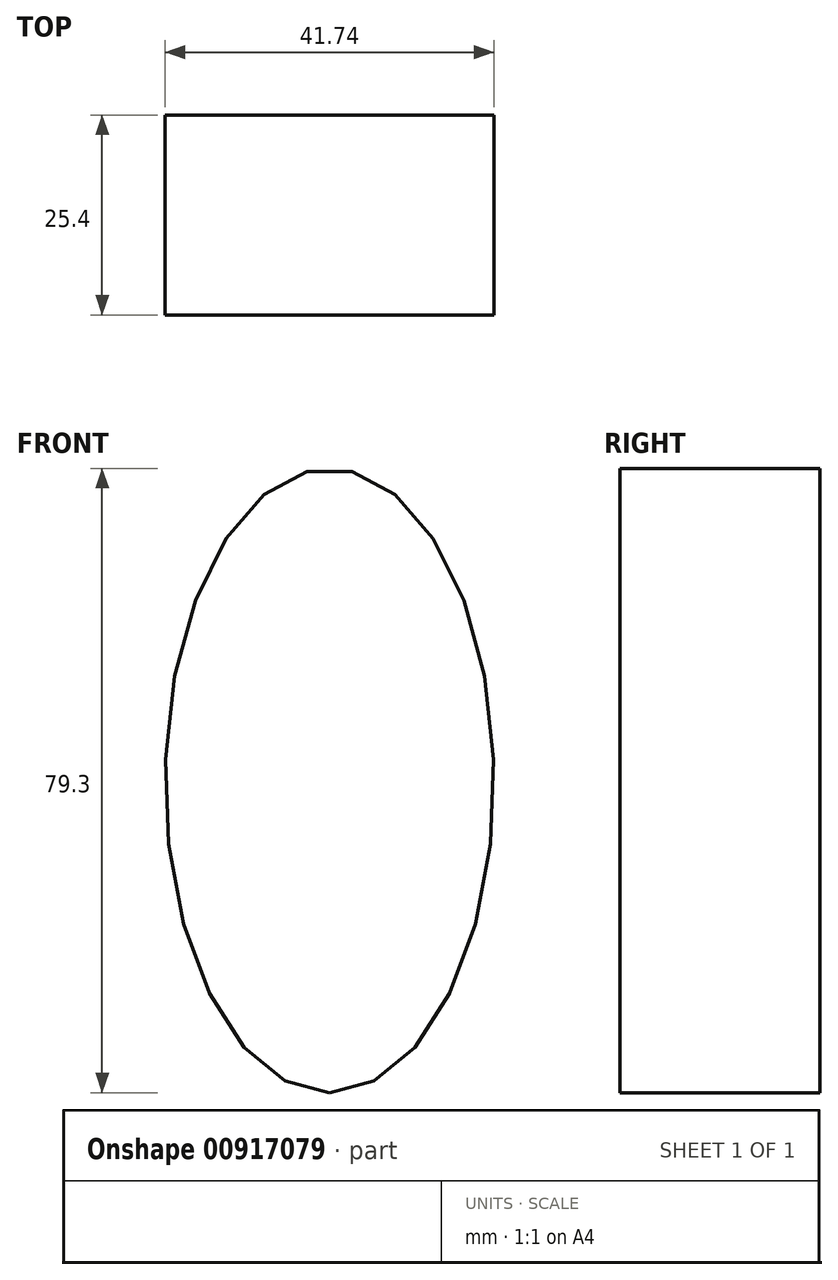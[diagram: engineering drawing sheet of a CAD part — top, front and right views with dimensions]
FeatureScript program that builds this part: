
annotation { "Feature Type Name" : "Feature", "Feature Type Description" : "" }
export const myFeature = defineFeature(function(context is Context, id is Id, definition is map)
    precondition{}
    {
        {
            var Q0;
            Q0=qCreatedBy(makeId("Front.planeOp"),FACE);
            var sketch = newSketch(context, id + "F0", { "sketchPlane" : qUnion([Q0])});
            skEllipse(sketch, "E0", {"center": v(0, 0) * mm, "majorRadius": 39.65 * mm, "minorRadius": 20.87 * mm, "majorAxis": v(0, -1)});
            skSolve(sketch);
        }
        {
            var Q0;
            Q0 = qSketchRegion(id + "F0", true);
            extrude(context, id + "F1", {"entities" : qUnion([Q0]), "depth" : 25.4 * mm, "offsetDistance" : 25.4 * mm});
        }
    });
